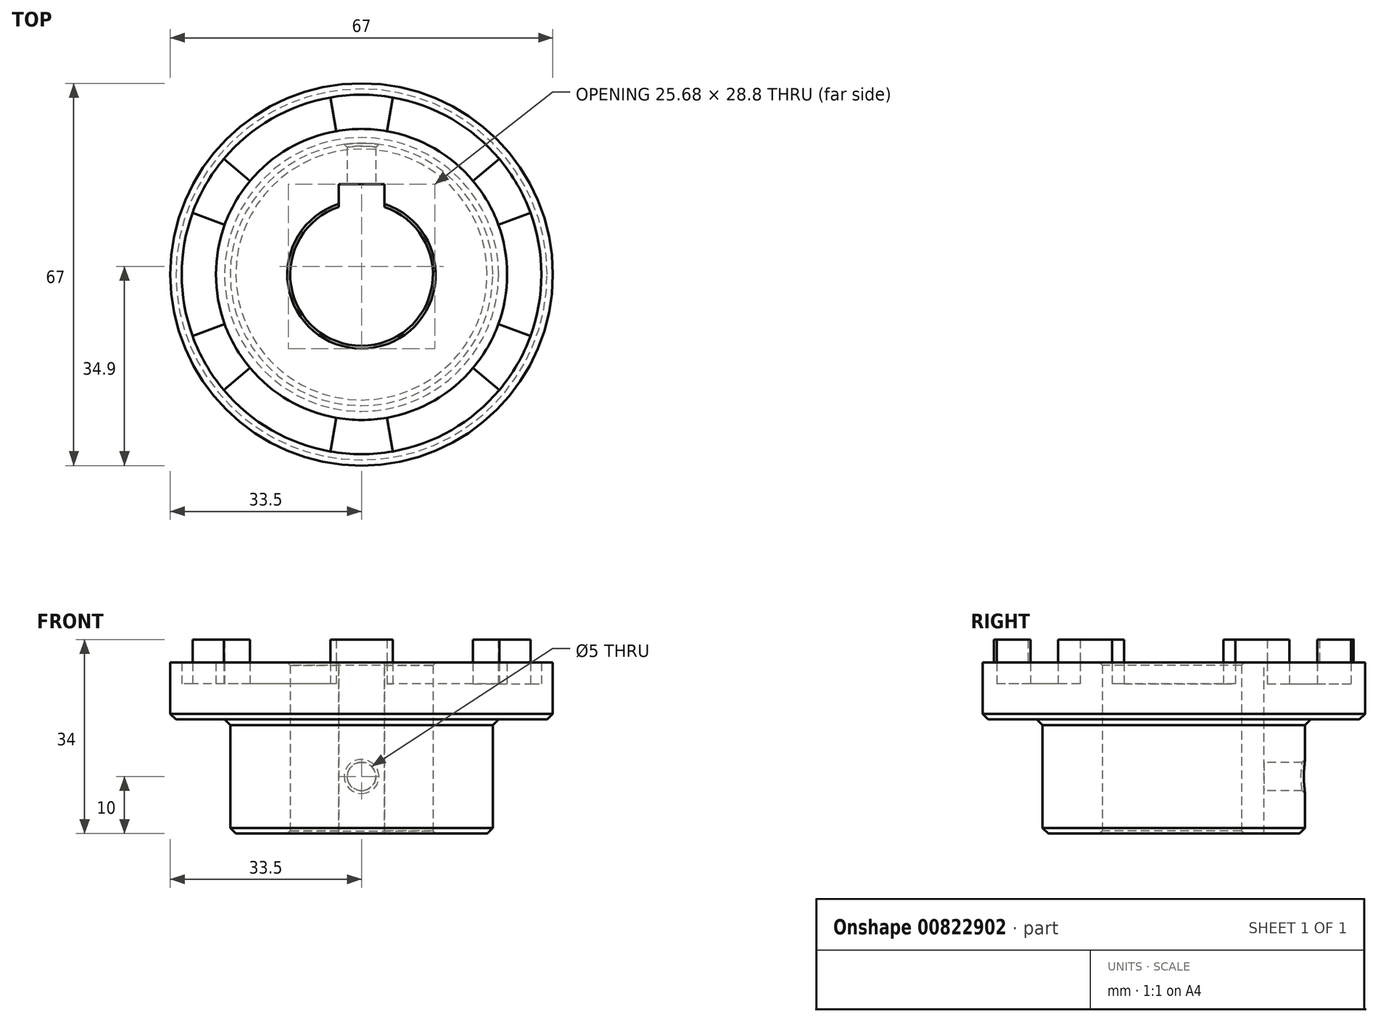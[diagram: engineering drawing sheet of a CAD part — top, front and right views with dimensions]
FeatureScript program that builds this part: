
annotation { "Feature Type Name" : "Feature", "Feature Type Description" : "" }
export const myFeature = defineFeature(function(context is Context, id is Id, definition is map)
    precondition{}
    {
        {
            var Q0;
            Q0=qCreatedBy(makeId("Front.planeOp"),FACE);
            var sketch = newSketch(context, id + "F0", { "sketchPlane" : qUnion([Q0])});
            skLineSegment(sketch, "E0", {"start": v(0, 0) * mm, "end": v(-12.5, 0) * mm, "construction": true});
            skLineSegment(sketch, "E1", {"start": v(-12.5, 0) * mm, "end": v(-12.5, 30) * mm});
            skLineSegment(sketch, "E2", {"start": v(-12.5, 30) * mm, "end": v(-25.5, 30) * mm});
            skLineSegment(sketch, "E3", {"start": v(-25.5, 30) * mm, "end": v(-25.5, 26.25) * mm});
            skLineSegment(sketch, "E4", {"start": v(-25.5, 26.25) * mm, "end": v(-31.5, 26.25) * mm});
            skLineSegment(sketch, "E5", {"start": v(-31.5, 26.25) * mm, "end": v(-31.5, 30) * mm});
            skLineSegment(sketch, "E6", {"start": v(-31.5, 30) * mm, "end": v(-33.5, 30) * mm});
            skLineSegment(sketch, "E7", {"start": v(-33.5, 30) * mm, "end": v(-33.5, 20) * mm});
            skLineSegment(sketch, "E8", {"start": v(-33.5, 20) * mm, "end": v(-23, 20) * mm});
            skLineSegment(sketch, "E9", {"start": v(-23, 20) * mm, "end": v(-23, 0) * mm});
            skLineSegment(sketch, "E10", {"start": v(-23, 0) * mm, "end": v(-12.5, 0) * mm});
            skLineSegment(sketch, "E11", {"start": v(0, 0) * mm, "end": v(0, 30) * mm, "construction": true});
            skSolve(sketch);
        }
        {
            var Q0;
            Q0=makeQuery(id+"F0.imprint","IMPRINT",FACE,{"disambiguationData":[TD([[makeQuery(id+"F0.imprint","IMPRINT",EDGE,{"derivedFrom":sQuery(id+"F0.wireOp",EDGE,"E1")}),1.0]])]});
            var Q1;
            Q1=sQuery(id+"F0.wireOp",EDGE,"E11");
            revolve(context, id + "F1", {"surfaceOperationType" : NewSurfaceOperationType.NEW, "entities" : qUnion([Q0]), "axis" : qUnion([Q1]), "revolveType" : RevolveType.FULL});
        }
        {
            var Q0;
            Q0=makeQuery(id+"F1.opRevolve","SWEPT_FACE",FACE,{"disambiguationData":[OSD([sQuery(id+"F0.wireOp",EDGE,"E8")])]});
            var Q1;
            Q1=makeQuery(id+"F1.opRevolve","SWEPT_EDGE",EDGE,{"disambiguationData":[OSD([sQuery(id+"F0.wireOp",EDGE,"E9"),sQuery(id+"F0.wireOp",EDGE,"E10")])]});
            chamfer(context, id + "F2", {"entities" : qUnion([Q0, Q1]), "width" : 1 * mm, "tangentPropagation" : true});
        }
        {
            var Q0;
            Q0=makeQuery(id+"F1.opRevolve","SWEPT_FACE",FACE,{"disambiguationData":[OSD([sQuery(id+"F0.wireOp",EDGE,"E1")])]});
            chamfer(context, id + "F3", {"entities" : qUnion([Q0]), "width" : 0.5 * mm, "tangentPropagation" : true});
        }
        {
            var Q0;
            Q0=makeQuery(id+"F1.opRevolve","SWEPT_FACE",FACE,{"disambiguationData":[OSD([sQuery(id+"F0.wireOp",EDGE,"E4")])]});
            var sketch = newSketch(context, id + "F4", { "sketchPlane" : qUnion([Q0])});
            skLineSegment(sketch, "E12", {"start": v(0, 0) * mm, "end": v(10.27, 0) * mm, "construction": true});
            skLineSegment(sketch, "E13.1.0", {"start": v(0, 0) * mm, "end": v(0, 10.27) * mm, "construction": true});
            skLineSegment(sketch, "E13.2.0", {"start": v(0, 0) * mm, "end": v(-10.27, 0) * mm, "construction": true});
            skLineSegment(sketch, "E13.3.0", {"start": v(0, 0) * mm, "end": v(0, -10.27) * mm, "construction": true});
            skPoint(sketch, "E13.center", {"position": v(0, 0) * mm});
            skLineSegment(sketch, "E14", {"start": v(0, 0) * mm, "end": v(47.61, 27.49) * mm, "construction": true});
            skLineSegment(sketch, "E15", {"start": v(19.53, 16.4) * mm, "end": v(24.13, 20.25) * mm});
            skLineSegment(sketch, "E16.MirrorCS", {"start": v(23.96, 8.72) * mm, "end": v(29.6, 10.77) * mm});
            skArc(sketch, "E17.0", {"start": v(23.96, 8.72) * mm, "mid": v(22.08, 12.75) * mm, "end": v(19.53, 16.4) * mm});
            skPoint(sketch, "E18.orphan", {"position": v(30.04, 25.2) * mm});
            skPoint(sketch, "E19.orphan", {"position": v(36.85, 13.41) * mm});
            skArc(sketch, "E20.0", {"start": v(29.6, 10.77) * mm, "mid": v(27.28, 15.75) * mm, "end": v(24.13, 20.25) * mm});
            skArc(sketch, "E21.1.0", {"start": v(4.43, 25.11) * mm, "mid": v(0, 25.5) * mm, "end": v(-4.43, 25.11) * mm});
            skLineSegment(sketch, "E21.1.1", {"start": v(-4.43, 25.11) * mm, "end": v(-5.47, 31.02) * mm});
            skLineSegment(sketch, "E21.1.2", {"start": v(4.43, 25.11) * mm, "end": v(5.47, 31.02) * mm});
            skArc(sketch, "E21.1.3", {"start": v(5.47, 31.02) * mm, "mid": v(0, 31.5) * mm, "end": v(-5.47, 31.02) * mm});
            skArc(sketch, "E21.2.0", {"start": v(-19.53, 16.4) * mm, "mid": v(-22.08, 12.75) * mm, "end": v(-23.96, 8.72) * mm});
            skLineSegment(sketch, "E21.2.1", {"start": v(-23.96, 8.72) * mm, "end": v(-29.6, 10.77) * mm});
            skLineSegment(sketch, "E21.2.2", {"start": v(-19.53, 16.4) * mm, "end": v(-24.13, 20.25) * mm});
            skArc(sketch, "E21.2.3", {"start": v(-24.13, 20.25) * mm, "mid": v(-27.28, 15.75) * mm, "end": v(-29.6, 10.77) * mm});
            skArc(sketch, "E21.3.0", {"start": v(-23.96, -8.72) * mm, "mid": v(-22.08, -12.75) * mm, "end": v(-19.53, -16.4) * mm});
            skLineSegment(sketch, "E21.3.1", {"start": v(-19.53, -16.4) * mm, "end": v(-24.13, -20.25) * mm});
            skLineSegment(sketch, "E21.3.2", {"start": v(-23.96, -8.72) * mm, "end": v(-29.6, -10.77) * mm});
            skArc(sketch, "E21.3.3", {"start": v(-29.6, -10.77) * mm, "mid": v(-27.28, -15.75) * mm, "end": v(-24.13, -20.25) * mm});
            skArc(sketch, "E21.4.0", {"start": v(-4.43, -25.11) * mm, "mid": v(0, -25.5) * mm, "end": v(4.43, -25.11) * mm});
            skLineSegment(sketch, "E21.4.1", {"start": v(4.43, -25.11) * mm, "end": v(5.47, -31.02) * mm});
            skLineSegment(sketch, "E21.4.2", {"start": v(-4.43, -25.11) * mm, "end": v(-5.47, -31.02) * mm});
            skArc(sketch, "E21.4.3", {"start": v(-5.47, -31.02) * mm, "mid": v(0, -31.5) * mm, "end": v(5.47, -31.02) * mm});
            skArc(sketch, "E21.5.0", {"start": v(19.53, -16.4) * mm, "mid": v(22.08, -12.75) * mm, "end": v(23.96, -8.72) * mm});
            skLineSegment(sketch, "E21.5.1", {"start": v(23.96, -8.72) * mm, "end": v(29.6, -10.77) * mm});
            skLineSegment(sketch, "E21.5.2", {"start": v(19.53, -16.4) * mm, "end": v(24.13, -20.25) * mm});
            skArc(sketch, "E21.5.3", {"start": v(24.13, -20.25) * mm, "mid": v(27.28, -15.75) * mm, "end": v(29.6, -10.77) * mm});
            skSolve(sketch);
        }
        {
            var Q0;
            Q0 = qSketchRegion(id + "F4", true);
            extrude(context, id + "F5", {"entities" : qUnion([Q0]), "operationType" : NewBodyOperationType.ADD, "depth" : 7.75 * mm, "offsetDistance" : 25 * mm});
        }
        {
            var Q0;
            Q0=makeQuery(id+"F1.opRevolve","SWEPT_FACE",FACE,{"disambiguationData":[OSD([sQuery(id+"F0.wireOp",EDGE,"E2")])]});
            var sketch = newSketch(context, id + "F6", { "sketchPlane" : qUnion([Q0])});
            skLineSegment(sketch, "E22", {"start": v(0, 0) * mm, "end": v(13.63, 0) * mm, "construction": true});
            skLineSegment(sketch, "E23.1.0", {"start": v(0, 0) * mm, "end": v(0, 13.63) * mm, "construction": true});
            skLineSegment(sketch, "E23.2.0", {"start": v(0, 0) * mm, "end": v(-13.63, 0) * mm, "construction": true});
            skLineSegment(sketch, "E23.3.0", {"start": v(0, 0) * mm, "end": v(0, -13.63) * mm, "construction": true});
            skPoint(sketch, "E23.center", {"position": v(0, 0) * mm});
            skLineSegment(sketch, "E24.bottom", {"start": v(4, 15.8) * mm, "end": v(-4, 15.8) * mm});
            skLineSegment(sketch, "E24.top", {"start": v(4, 8.8) * mm, "end": v(-4, 8.8) * mm});
            skLineSegment(sketch, "E24.left", {"start": v(4, 15.8) * mm, "end": v(4, 8.8) * mm});
            skLineSegment(sketch, "E24.right", {"start": v(-4, 15.8) * mm, "end": v(-4, 8.8) * mm});
            skPoint(sketch, "E24.middle", {"position": v(0, 12.3) * mm});
            skCircle(sketch, "E25.0", {"center": v(0, 0) * mm, "radius": 12.5 * mm, "construction": true});
            skPoint(sketch, "E26", {"position": v(0, -12.5) * mm});
            skSolve(sketch);
        }
        {
            var Q0;
            Q0 = qSketchRegion(id + "F6", true);
            extrude(context, id + "F7", {"entities" : qUnion([Q0]), "operationType" : NewBodyOperationType.REMOVE, "endBound" : BoundingType.UP_TO_NEXT, "oppositeDirection" : true, "depth" : 25 * mm, "offsetDistance" : 25 * mm});
        }
        {
            var Q0;
            Q0=qCreatedBy(makeId("Front.planeOp"),FACE);
            var sketch = newSketch(context, id + "F8", { "sketchPlane" : qUnion([Q0])});
            skLineSegment(sketch, "E27", {"start": v(0, 0) * mm, "end": v(0, 10) * mm, "construction": true});
            skCircle(sketch, "E28", {"center": v(0, 10) * mm, "radius": 2.5 * mm});
            skSolve(sketch);
        }
        {
            var Q0;
            Q0=makeQuery(id+"F8.imprint","IMPRINT",FACE,{"disambiguationData":[TD([[makeQuery(id+"F8.imprint","IMPRINT",EDGE,{"derivedFrom":sQuery(id+"F8.wireOp",EDGE,"E28")}),1.0]])]});
            extrude(context, id + "F9", {"entities" : qUnion([Q0]), "operationType" : NewBodyOperationType.REMOVE, "oppositeDirection" : true, "depth" : 25 * mm, "offsetDistance" : 25 * mm});
        }
        {
            var Q0;
            Q0=makeQuery(id+"F9.boolean.opBoolean","INTERSECT",EDGE,{"derivedFrom":[makeQuery(id+"F1.opRevolve","SWEPT_FACE",FACE,{"disambiguationData":[OSD([sQuery(id+"F0.wireOp",EDGE,"E9")])]}),makeQuery(id+"F9.opExtrude","SWEPT_FACE",FACE,{"disambiguationData":[OSD([sQuery(id+"F8.wireOp",EDGE,"E28")])]})]});
            chamfer(context, id + "F10", {"entities" : qUnion([Q0]), "width" : 0.5 * mm, "tangentPropagation" : true});
        }
    });
